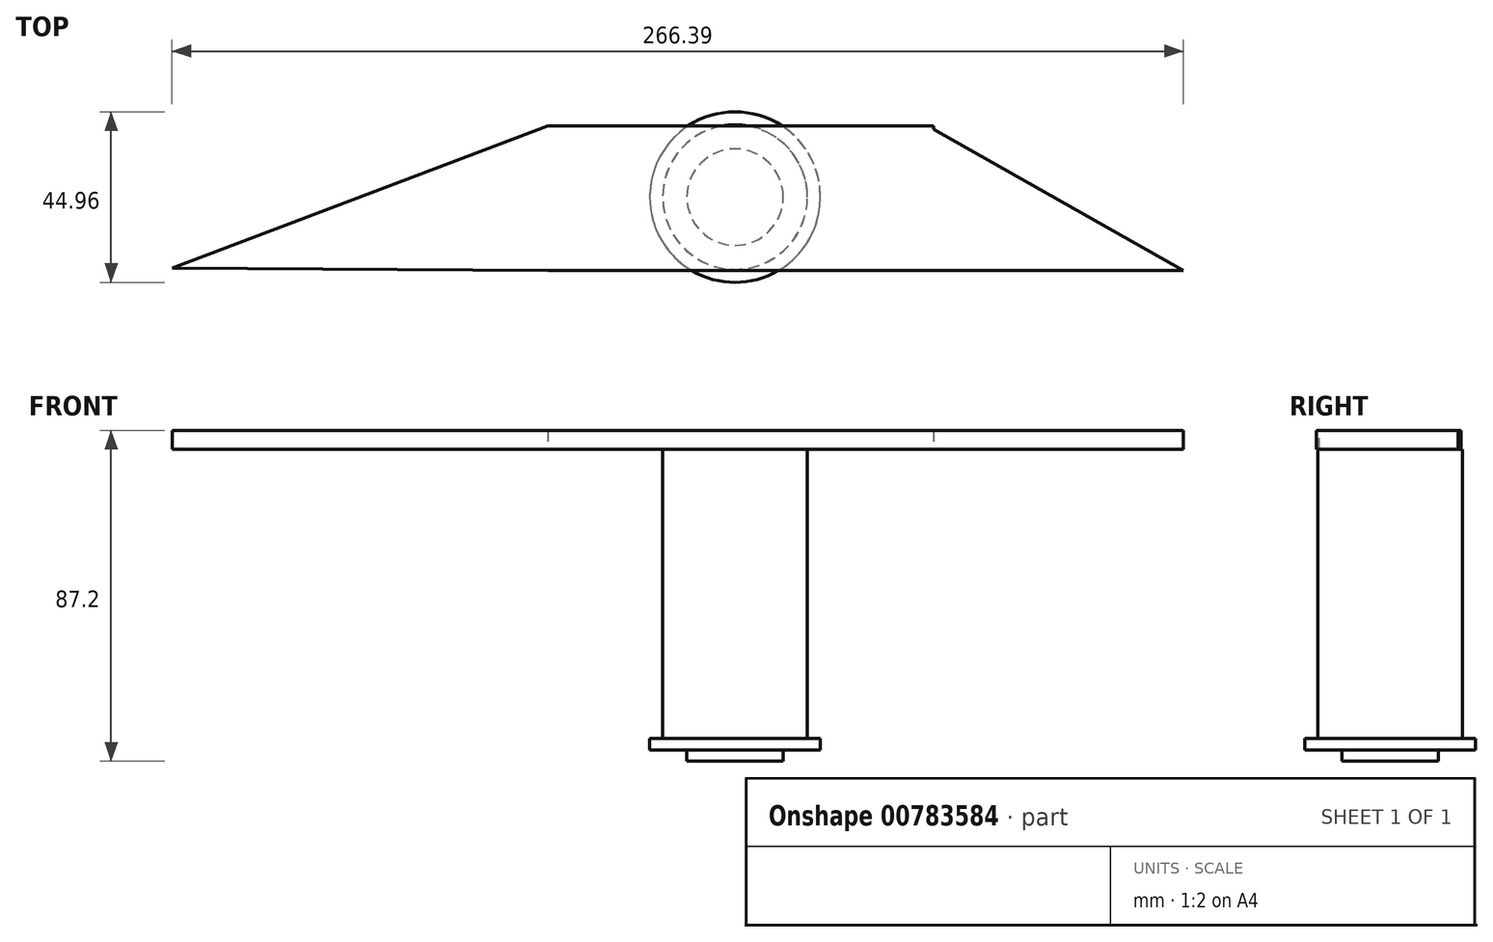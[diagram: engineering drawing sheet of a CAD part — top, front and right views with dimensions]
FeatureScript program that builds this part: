
annotation { "Feature Type Name" : "Feature", "Feature Type Description" : "" }
export const myFeature = defineFeature(function(context is Context, id is Id, definition is map)
    precondition{}
    {
        {
            var Q0;
            Q0=qCreatedBy(makeId("Top.planeOp"),FACE);
            var sketch = newSketch(context, id + "F0", { "sketchPlane" : qUnion([Q0])});
            skCircle(sketch, "E0", {"center": v(0, 0) * mm, "radius": 19.05 * mm});
            skSolve(sketch);
        }
        {
            var Q0;
            Q0 = qSketchRegion(id + "F0", true);
            extrude(context, id + "F1", {"entities" : qUnion([Q0]), "depth" : 76.2 * mm, "offsetDistance" : 25.4 * mm});
        }
        {
            var Q0;
            Q0=makeQuery(id+"F1.opExtrude","CAP_FACE",FACE,{"disambiguationData":[OSD([sQuery(id+"F0.wireOp",EDGE,"E0")])],"isStart":false});
            var sketch = newSketch(context, id + "F2", { "sketchPlane" : qUnion([Q0])});
            skLineSegment(sketch, "E1.bottom", {"start": v(-49.35, 18.72) * mm, "end": v(52.25, 18.72) * mm});
            skLineSegment(sketch, "E1.top", {"start": v(-49.35, -19.38) * mm, "end": v(52.25, -19.38) * mm});
            skLineSegment(sketch, "E1.left", {"start": v(-49.35, 18.72) * mm, "end": v(-49.35, -19.38) * mm});
            skLineSegment(sketch, "E1.right", {"start": v(52.25, 18.72) * mm, "end": v(52.25, -19.38) * mm});
            skSolve(sketch);
        }
        {
            var Q0;
            Q0 = qSketchRegion(id + "F2", true);
            extrude(context, id + "F3", {"entities" : qUnion([Q0]), "operationType" : NewBodyOperationType.ADD, "depth" : 5 * mm, "offsetDistance" : 25.4 * mm});
        }
        {
            var Q0;
            Q0=makeQuery(id+"F1.opExtrude","CAP_FACE",FACE,{"disambiguationData":[OSD([sQuery(id+"F0.wireOp",EDGE,"E0")])],"isStart":true});
            var sketch = newSketch(context, id + "F4", { "sketchPlane" : qUnion([Q0])});
            skCircle(sketch, "E2", {"center": v(0, 0) * mm, "radius": 22.48 * mm});
            skSolve(sketch);
        }
        {
            var Q0;
            Q0=makeQuery(id+"F4.imprint","IMPRINT",FACE,{"disambiguationData":[TD([[makeQuery(id+"F4.imprint","IMPRINT",EDGE,{"derivedFrom":sQuery(id+"F4.wireOp",EDGE,"E2")}),1.0]])]});
            var Q1;
            Q1=makeQuery(id+"F4.imprint","IMPRINT",FACE,{"disambiguationData":[TD([[makeQuery(id+"F4.imprint","IMPRINT",EDGE,{"derivedFrom":makeQuery(id+"F1.opExtrude","CAP_EDGE",EDGE,{"disambiguationData":[OSD([sQuery(id+"F0.wireOp",EDGE,"E0")])],"isStart":true})}),-1.0]])]});
            extrude(context, id + "F5", {"entities" : qUnion([Q0, Q1]), "operationType" : NewBodyOperationType.ADD, "depth" : 3 * mm, "offsetDistance" : 25.4 * mm});
        }
        {
            var Q0;
            Q0=makeQuery(id+"F5.opExtrude","CAP_FACE",FACE,{"disambiguationData":[OSD([sQuery(id+"F4.wireOp",EDGE,"E2")])],"isStart":false});
            var sketch = newSketch(context, id + "F6", { "sketchPlane" : qUnion([Q0])});
            skCircle(sketch, "E3", {"center": v(0, 0) * mm, "radius": 12.7 * mm});
            skSolve(sketch);
        }
        {
            var Q0;
            Q0=makeQuery(id+"F6.imprint","IMPRINT",FACE,{"disambiguationData":[TD([[makeQuery(id+"F6.imprint","IMPRINT",EDGE,{"derivedFrom":sQuery(id+"F6.wireOp",EDGE,"E3")}),1.0]])]});
            extrude(context, id + "F7", {"entities" : qUnion([Q0]), "operationType" : NewBodyOperationType.ADD, "depth" : 3 * mm, "offsetDistance" : 25.4 * mm});
        }
        {
            var Q0;
            Q0=makeQuery(id+"F3.opExtrude","CAP_FACE",FACE,{"disambiguationData":[OSD([sQuery(id+"F2.wireOp",EDGE,"E1.bottom"),sQuery(id+"F2.wireOp",EDGE,"E1.top"),sQuery(id+"F2.wireOp",EDGE,"E1.left"),sQuery(id+"F2.wireOp",EDGE,"E1.right")])],"isStart":false});
            var sketch = newSketch(context, id + "F8", { "sketchPlane" : qUnion([Q0])});
            skLineSegment(sketch, "E4", {"start": v(-49.35, 18.72) * mm, "end": v(-148.3, -18.69) * mm});
            skLineSegment(sketch, "E5", {"start": v(-148.3, -18.69) * mm, "end": v(-49.35, -19.38) * mm});
            skLineSegment(sketch, "E6", {"start": v(-49.35, -19.38) * mm, "end": v(52.25, -19.38) * mm});
            skLineSegment(sketch, "E7", {"start": v(52.25, -19.38) * mm, "end": v(118.08, -19.38) * mm});
            skLineSegment(sketch, "E8", {"start": v(118.08, -19.38) * mm, "end": v(52.25, 17.85) * mm});
            skSolve(sketch);
        }
        {
            var Q0;
            Q0=makeQuery(id+"F8.imprint","IMPRINT",FACE,{"disambiguationData":[TD([[makeQuery(id+"F8.imprint","IMPRINT",EDGE,{"derivedFrom":sQuery(id+"F8.wireOp",EDGE,"E4")}),1.0]])]});
            var Q1;
            {var subQ0=sQuery(id+"F8.wireOp",EDGE,"E7");Q1=makeQuery(id+"F8.imprint","IMPRINT",FACE,{"disambiguationData":[TD([[makeQuery(id+"F8.imprint","IMPRINT",EDGE,{"derivedFrom":subQ0}),1.0]])]});}
            extrude(context, id + "F9", {"entities" : qUnion([Q0, Q1]), "operationType" : NewBodyOperationType.ADD, "oppositeDirection" : true, "depth" : 5 * mm, "offsetDistance" : 25.4 * mm});
        }
    });
